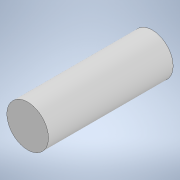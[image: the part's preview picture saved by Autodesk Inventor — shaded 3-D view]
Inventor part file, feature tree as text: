
AUTODESK INVENTOR PART (.ipt)
format: ipt  version: 2022 (Build 260153000, 153)  size: 90,624 bytes
history: native  units: in
note: dims shown in document units (in); Inventor stores cm internally (conversion verified against a paired STEP export)
features: extrude x1, sketch x1
ambient origin geometry x8: Origin, YZ Plane, XZ Plane, XY Plane, X Axis, Y Axis, Z Axis, Center Point
bodies: Solid1 (feature_tree)
feature tree (2):
  extrude  "Extrusion1"  Depth=96.0in TaperAngle=0.0deg
  sketch  "Sketch1"  dims[d0=32.0in d1=96.0in d2=0.0in]
